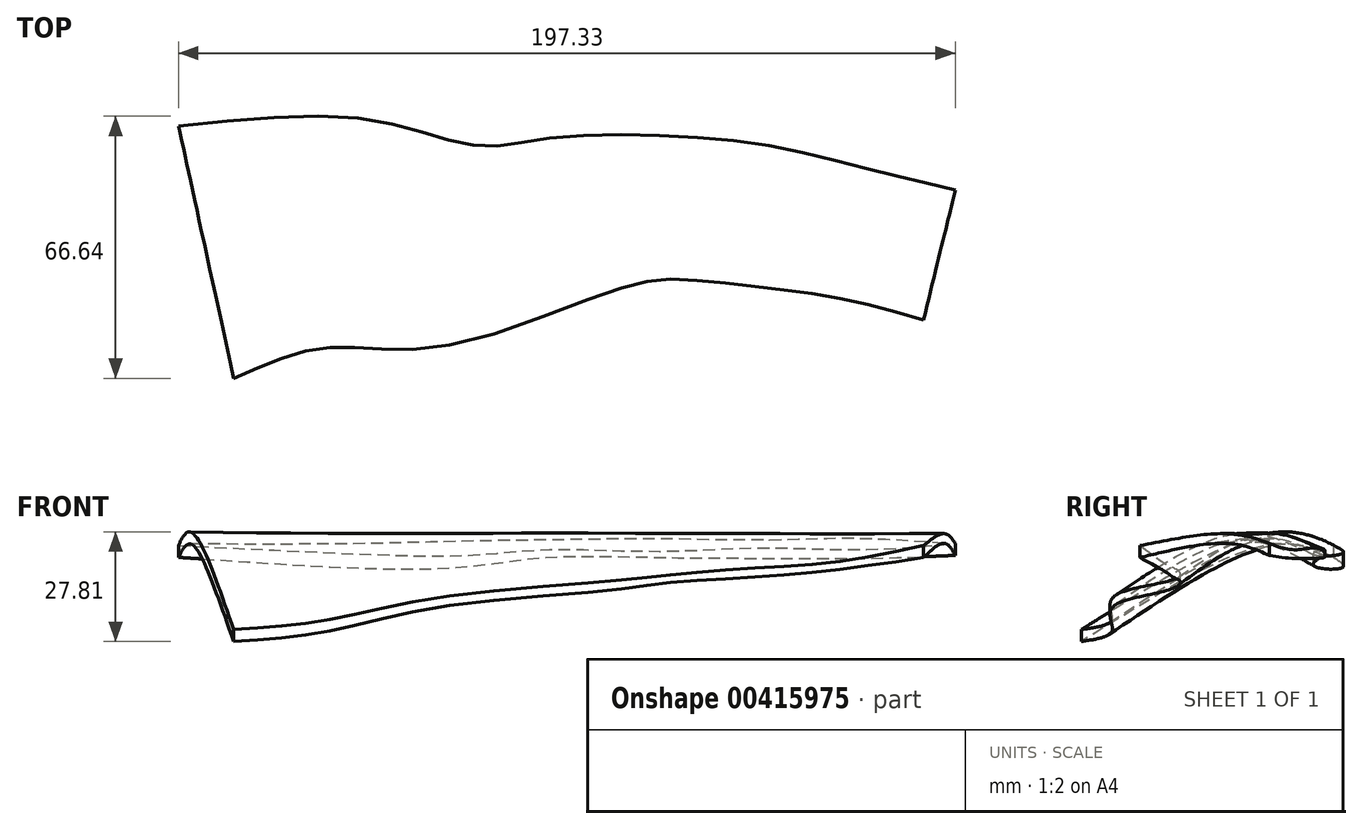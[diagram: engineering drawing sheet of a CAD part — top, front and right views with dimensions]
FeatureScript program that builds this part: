
annotation { "Feature Type Name" : "Feature", "Feature Type Description" : "" }
export const myFeature = defineFeature(function(context is Context, id is Id, definition is map)
    precondition{}
    {
        {
            var Q0;
            Q0=qCreatedBy(makeId("Top.planeOp"),FACE);
            var sketch = newSketch(context, id + "F0", { "sketchPlane" : qUnion([Q0])});
            skFitSpline(sketch, "E0", {"points": [v(0, 0) * mm, v(39.03, 3.4) * mm, v(55.33, -2.19) * mm, v(73.53, -7.45) * mm, v(96.2, -4.17) * mm, v(120, 0) * mm, v(143.3, -0.7) * mm, v(165.12, -3.6) * mm, v(191, -9.56) * mm], "startDerivative": vector(199.57, 43.61) * mm, "endDerivative": vector(144.28, -35.3) * mm});
            skSolve(sketch);
        }
        {
            var Q0;
            Q0=sQuery(id+"F0.wireOp",VERTEX,"E0.start");
            var Q1;
            Q1=sQuery(id+"F0.wireOp",EDGE,"E0");
            cPlane(context, id + "F1", {"entities" : qUnion([Q0, Q1]), "cplaneType" : CPlaneType.CURVE_POINT, "offset" : 25.4 * mm, "width" : 152.4 * mm, "height" : 152.4 * mm});
        }
        {
            var Q0;
            Q0=qCreatedBy(id+"F1.planeOp",FACE);
            var sketch = newSketch(context, id + "F2", { "sketchPlane" : qUnion([Q0])});
            skFitSpline(sketch, "E1", {"points": [v(17.6, -3) * mm, v(0, 0) * mm, v(-48, -24.35) * mm], "startDerivative": vector(-42.39, 22.1) * mm, "endDerivative": vector(-85.1, -51.75) * mm});
            skFitSpline(sketch, "E2", {"points": [v(17.6, -6) * mm, v(0, -3) * mm, v(-48, -27.35) * mm], "startDerivative": vector(-42.52, 19.98) * mm, "endDerivative": vector(-84.97, -50.55) * mm});
            skLineSegment(sketch, "E3", {"start": v(17.6, -3) * mm, "end": v(17.6, -6) * mm});
            skLineSegment(sketch, "E4", {"start": v(-48, -24.35) * mm, "end": v(-48, -27.35) * mm});
            skSolve(sketch);
        }
        {
            var Q0;
            Q0=sQuery(id+"F0.wireOp",VERTEX,"E0.1.internal");
            var Q1;
            Q1=sQuery(id+"F0.wireOp",EDGE,"E0");
            cPlane(context, id + "F3", {"entities" : qUnion([Q0, Q1]), "cplaneType" : CPlaneType.CURVE_POINT, "offset" : 25 * mm, "width" : 150 * mm, "height" : 150 * mm});
        }
        {
            var Q0;
            Q0=qCreatedBy(id+"F3.planeOp",FACE);
            var sketch = newSketch(context, id + "F4", { "sketchPlane" : qUnion([Q0])});
            skPoint(sketch, "E5.0", {"position": v(7.9, 0) * mm});
            skFitSpline(sketch, "E6", {"points": [v(23.92, -5.1) * mm, v(7.9, 0) * mm, v(-34.9, -21.9) * mm], "startDerivative": vector(-38.47, 22.75) * mm, "endDerivative": vector(-75.96, -50.1) * mm});
            skFitSpline(sketch, "E7", {"points": [v(23.92, -8.69) * mm, v(7.9, -2.59) * mm, v(-34.9, -24.77) * mm], "startDerivative": vector(-38.14, 26) * mm, "endDerivative": vector(-76.28, -51.62) * mm});
            skLineSegment(sketch, "E8", {"start": v(23.92, -5.1) * mm, "end": v(23.92, -8.69) * mm});
            skLineSegment(sketch, "E9", {"start": v(-34.9, -21.9) * mm, "end": v(-34.9, -24.77) * mm});
            skSolve(sketch);
        }
        {
            var Q0;
            Q0=sQuery(id+"F0.wireOp",VERTEX,"E0.3.internal");
            var Q1;
            Q1=sQuery(id+"F0.wireOp",EDGE,"E0");
            cPlane(context, id + "F5", {"entities" : qUnion([Q0, Q1]), "cplaneType" : CPlaneType.CURVE_POINT, "offset" : 25 * mm, "width" : 150 * mm, "height" : 150 * mm});
        }
        {
            var Q0;
            Q0=qCreatedBy(id+"F5.planeOp",FACE);
            var sketch = newSketch(context, id + "F6", { "sketchPlane" : qUnion([Q0])});
            skPoint(sketch, "E10.0", {"position": v(-2.82, 0) * mm});
            skFitSpline(sketch, "E11", {"points": [v(16.7, -5.18) * mm, v(-2.82, 0) * mm, v(-32.4, -14.98) * mm], "startDerivative": vector(-42.76, 20.26) * mm, "endDerivative": vector(-54.93, -37.5) * mm});
            skFitSpline(sketch, "E12", {"points": [v(16.7, -7.81) * mm, v(-2.82, -1.91) * mm, v(-32.4, -17.38) * mm], "startDerivative": vector(-42.7, 22.44) * mm, "endDerivative": vector(-54.99, -39.06) * mm});
            skLineSegment(sketch, "E13", {"start": v(16.7, -5.18) * mm, "end": v(16.7, -7.81) * mm});
            skLineSegment(sketch, "E14", {"start": v(-32.4, -14.98) * mm, "end": v(-32.4, -17.38) * mm});
            skSolve(sketch);
        }
        {
            var Q0;
            Q0=sQuery(id+"F0.wireOp",EDGE,"E0");
            cPoint(context, id + "F7", {"entities" : qUnion([Q0]), "parameter" : 0.5});
        }
        {
            var Q0;
            Q0 = qCreatedBy(id + "F7" ,VERTEX);
            var Q1;
            Q1=sQuery(id+"F0.wireOp",EDGE,"E0");
            cPlane(context, id + "F8", {"entities" : qUnion([Q0, Q1]), "cplaneType" : CPlaneType.CURVE_POINT, "offset" : 25 * mm, "width" : 150 * mm, "height" : 150 * mm});
        }
        {
            var Q0;
            Q0=qCreatedBy(id+"F8.planeOp",FACE);
            var sketch = newSketch(context, id + "F9", { "sketchPlane" : qUnion([Q0])});
            skPoint(sketch, "E15.0", {"position": v(-26.22, 0) * mm});
            skFitSpline(sketch, "E16", {"points": [v(-7.05, -3.98) * mm, v(-26.22, 0) * mm, v(-49.25, -12.51) * mm], "startDerivative": vector(-41.2, 16) * mm, "endDerivative": vector(-43.4, -31.92) * mm});
            skFitSpline(sketch, "E17", {"points": [v(-7.05, -5.9) * mm, v(-26.22, -1.75) * mm, v(-49.25, -14.9) * mm], "startDerivative": vector(-40.92, 16.69) * mm, "endDerivative": vector(-43.2, -33.42) * mm});
            skLineSegment(sketch, "E18", {"start": v(-7.05, -3.98) * mm, "end": v(-7.05, -5.9) * mm});
            skLineSegment(sketch, "E19", {"start": v(-49.25, -12.51) * mm, "end": v(-49.25, -14.9) * mm});
            skSolve(sketch);
        }
        {
            var Q0;
            Q0=sQuery(id+"F0.wireOp",VERTEX,"E0.5.internal");
            var Q1;
            Q1=sQuery(id+"F0.wireOp",EDGE,"E0");
            cPlane(context, id + "F10", {"entities" : qUnion([Q0, Q1]), "cplaneType" : CPlaneType.CURVE_POINT, "offset" : 25 * mm, "width" : 150 * mm, "height" : 150 * mm});
        }
        {
            var Q0;
            Q0=qCreatedBy(id+"F10.planeOp",FACE);
            var sketch = newSketch(context, id + "F11", { "sketchPlane" : qUnion([Q0])});
            skPoint(sketch, "E20.0", {"position": v(-8.35, 0) * mm});
            skFitSpline(sketch, "E21", {"points": [v(6.49, -4.46) * mm, v(-8.35, 0) * mm, v(-30.1, -10.43) * mm], "startDerivative": vector(-32.05, 16.42) * mm, "endDerivative": vector(-40.8, -26.77) * mm});
            skFitSpline(sketch, "E22", {"points": [v(6.49, -6.02) * mm, v(-8.35, -1.37) * mm, v(-30.1, -12.37) * mm], "startDerivative": vector(-32.14, 17.17) * mm, "endDerivative": vector(-40.71, -28.18) * mm});
            skLineSegment(sketch, "E23", {"start": v(6.49, -4.46) * mm, "end": v(6.49, -6.02) * mm});
            skLineSegment(sketch, "E24", {"start": v(-30.1, -10.43) * mm, "end": v(-30.1, -12.37) * mm});
            skSolve(sketch);
        }
        {
            var Q0;
            Q0=sQuery(id+"F0.wireOp",VERTEX,"E0.6.internal");
            var Q1;
            Q1=sQuery(id+"F0.wireOp",EDGE,"E0");
            cPlane(context, id + "F12", {"entities" : qUnion([Q0, Q1]), "cplaneType" : CPlaneType.CURVE_POINT, "offset" : 25 * mm, "width" : 150 * mm, "height" : 150 * mm});
        }
        {
            var Q0;
            Q0=qCreatedBy(id+"F12.planeOp",FACE);
            var sketch = newSketch(context, id + "F13", { "sketchPlane" : qUnion([Q0])});
            skPoint(sketch, "E25.0", {"position": v(12.12, 0) * mm});
            skFitSpline(sketch, "E26", {"points": [v(25.39, -3.57) * mm, v(12.12, 0) * mm, v(-10.67, -8.71) * mm], "startDerivative": vector(-28.03, 13.17) * mm, "endDerivative": vector(-42.3, -21.85) * mm});
            skFitSpline(sketch, "E27", {"points": [v(25.39, -6.25) * mm, v(12.12, -1.68) * mm, v(-10.67, -11.13) * mm], "startDerivative": vector(-27.88, 16.47) * mm, "endDerivative": vector(-42.44, -24.35) * mm});
            skLineSegment(sketch, "E28", {"start": v(25.39, -3.57) * mm, "end": v(25.39, -6.25) * mm});
            skLineSegment(sketch, "E29", {"start": v(-10.67, -8.71) * mm, "end": v(-10.67, -11.13) * mm});
            skSolve(sketch);
        }
        {
            var Q0;
            Q0=sQuery(id+"F0.wireOp",VERTEX,"E0.7.internal");
            var Q1;
            Q1=sQuery(id+"F0.wireOp",EDGE,"E0");
            cPlane(context, id + "F14", {"entities" : qUnion([Q0, Q1]), "cplaneType" : CPlaneType.CURVE_POINT, "offset" : 25 * mm, "width" : 150 * mm, "height" : 150 * mm});
        }
        {
            var Q0;
            Q0=qCreatedBy(id+"F14.planeOp",FACE);
            var sketch = newSketch(context, id + "F15", { "sketchPlane" : qUnion([Q0])});
            skPoint(sketch, "E30.0", {"position": v(27.52, 0) * mm});
            skFitSpline(sketch, "E31", {"points": [v(38.75, -4.07) * mm, v(27.52, 0) * mm, v(4.81, -7.48) * mm], "startDerivative": vector(-24.7, 14.52) * mm, "endDerivative": vector(-42.17, -19.4) * mm});
            skFitSpline(sketch, "E32", {"points": [v(38.75, -6.3) * mm, v(27.52, -1.23) * mm, v(4.81, -9.43) * mm], "startDerivative": vector(-24.44, 17.63) * mm, "endDerivative": vector(-42.43, -21.7) * mm});
            skLineSegment(sketch, "E33", {"start": v(38.75, -4.07) * mm, "end": v(38.75, -6.3) * mm});
            skLineSegment(sketch, "E34", {"start": v(4.81, -7.48) * mm, "end": v(4.81, -9.43) * mm});
            skSolve(sketch);
        }
        {
            var Q0;
            Q0=sQuery(id+"F0.wireOp",VERTEX,"E0.end");
            var Q1;
            Q1=sQuery(id+"F0.wireOp",EDGE,"E0");
            cPlane(context, id + "F16", {"entities" : qUnion([Q0, Q1]), "cplaneType" : CPlaneType.CURVE_POINT, "offset" : 25 * mm, "width" : 150 * mm, "height" : 150 * mm});
        }
        {
            var Q0;
            Q0=qCreatedBy(id+"F16.planeOp",FACE);
            var sketch = newSketch(context, id + "F17", { "sketchPlane" : qUnion([Q0])});
            skPoint(sketch, "E35.0", {"position": v(36.1, 0) * mm});
            skFitSpline(sketch, "E36", {"points": [v(46.9, -2.46) * mm, v(36.1, 0) * mm, v(12.97, -3.03) * mm], "startDerivative": vector(-23.91, 8.32) * mm, "endDerivative": vector(-42.8, -8.43) * mm});
            skFitSpline(sketch, "E37", {"points": [v(46.9, -5.5) * mm, v(36.1, -2.46) * mm, v(12.97, -6.07) * mm], "startDerivative": vector(-23.8, 10.18) * mm, "endDerivative": vector(-42.9, -10.09) * mm});
            skLineSegment(sketch, "E38", {"start": v(46.9, -2.46) * mm, "end": v(46.9, -5.5) * mm});
            skLineSegment(sketch, "E39", {"start": v(12.97, -3.03) * mm, "end": v(12.97, -6.07) * mm});
            skSolve(sketch);
        }
        {
            var Q0;
            Q0 = qSketchRegion(id + "F2", true);
            var Q1;
            Q1 = qSketchRegion(id + "F4", true);
            var Q2;
            Q2 = qSketchRegion(id + "F6", true);
            var Q3;
            Q3 = qSketchRegion(id + "F9", true);
            var Q4;
            Q4 = qSketchRegion(id + "F11", true);
            var Q5;
            Q5 = qSketchRegion(id + "F13", true);
            var Q6;
            Q6 = qSketchRegion(id + "F15", true);
            var Q7;
            Q7 = qSketchRegion(id + "F17", true);
            loft(context, id + "F18", {"sheetProfilesArray" : [{ "sheetProfileEntities" : qUnion([Q0]) }, { "sheetProfileEntities" : qUnion([Q1]) }, { "sheetProfileEntities" : qUnion([Q2]) }, { "sheetProfileEntities" : qUnion([Q3]) }, { "sheetProfileEntities" : qUnion([Q4]) }, { "sheetProfileEntities" : qUnion([Q5]) }, { "sheetProfileEntities" : qUnion([Q6]) }, { "sheetProfileEntities" : qUnion([Q7]) }]});
        }
    });
